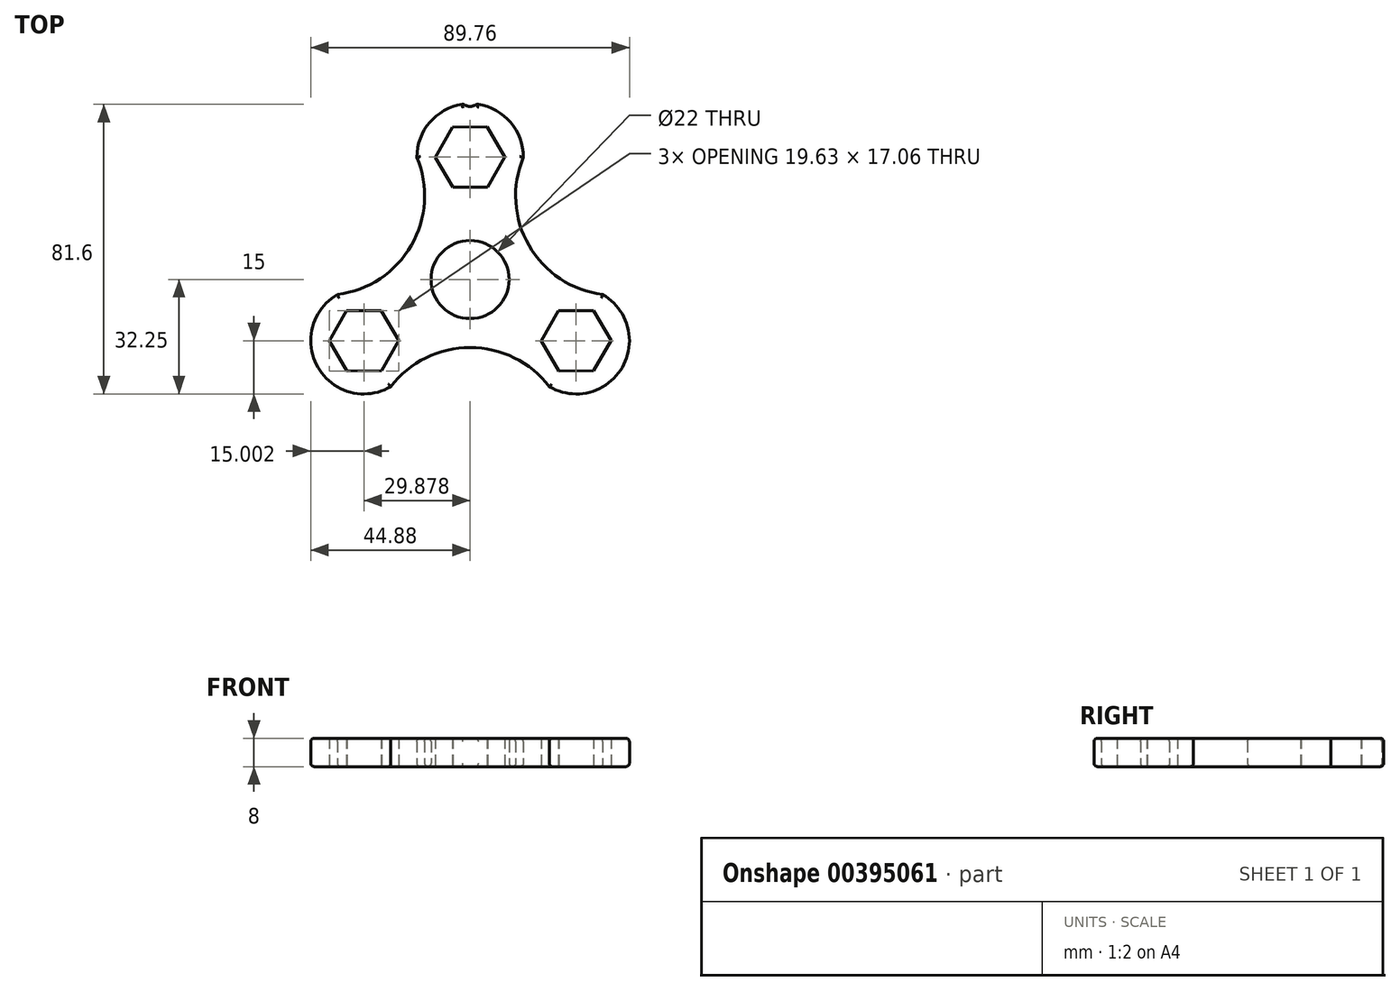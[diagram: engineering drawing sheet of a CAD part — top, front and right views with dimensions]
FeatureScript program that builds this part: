
annotation { "Feature Type Name" : "Feature", "Feature Type Description" : "" }
export const myFeature = defineFeature(function(context is Context, id is Id, definition is map)
    precondition{}
    {
        {
            var Q0;
            Q0=qCreatedBy(makeId("Top.planeOp"),FACE);
            var sketch = newSketch(context, id + "F0", { "sketchPlane" : qUnion([Q0])});
            skCircle(sketch, "E0", {"center": v(0, 0) * mm, "radius": 11 * mm});
            skCircle(sketch, "E1.cCircle", {"center": v(0, 34.5) * mm, "radius": 8.5 * mm, "construction": true});
            skLineSegment(sketch, "E1.0", {"start": v(9.81, 34.56) * mm, "end": v(4.96, 26.03) * mm});
            skLineSegment(sketch, "E1.1", {"start": v(4.96, 26.03) * mm, "end": v(-4.86, 25.97) * mm});
            skLineSegment(sketch, "E1.2", {"start": v(-4.86, 25.97) * mm, "end": v(-9.81, 34.44) * mm});
            skLineSegment(sketch, "E1.3", {"start": v(-9.81, 34.44) * mm, "end": v(-4.96, 42.97) * mm});
            skLineSegment(sketch, "E1.4", {"start": v(-4.96, 42.97) * mm, "end": v(4.86, 43.03) * mm});
            skLineSegment(sketch, "E1.5", {"start": v(4.86, 43.03) * mm, "end": v(9.81, 34.56) * mm});
            skPoint(sketch, "E1.0.midPoint", {"position": v(7.39, 30.3) * mm});
            skArc(sketch, "E2", {"start": v(15, 34.44) * mm, "mid": v(0, 49.5) * mm, "end": v(-15, 34.44) * mm});
            skArc(sketch, "E3.1.0", {"start": v(-37.33, -4.23) * mm, "mid": v(-42.87, -24.75) * mm, "end": v(-22.33, -30.21) * mm});
            skLineSegment(sketch, "E3.1.3", {"start": v(-34.84, -8.78) * mm, "end": v(-25.02, -8.72) * mm});
            skLineSegment(sketch, "E3.1.4", {"start": v(-39.7, -17.31) * mm, "end": v(-34.84, -8.78) * mm});
            skLineSegment(sketch, "E3.1.5", {"start": v(-34.73, -25.78) * mm, "end": v(-39.7, -17.31) * mm});
            skLineSegment(sketch, "E3.1.6", {"start": v(-24.92, -25.72) * mm, "end": v(-34.73, -25.78) * mm});
            skLineSegment(sketch, "E3.1.7", {"start": v(-20.06, -17.19) * mm, "end": v(-24.92, -25.72) * mm});
            skLineSegment(sketch, "E3.1.8", {"start": v(-25.02, -8.72) * mm, "end": v(-20.06, -17.19) * mm});
            skArc(sketch, "E3.2.0", {"start": v(22.33, -30.21) * mm, "mid": v(42.87, -24.75) * mm, "end": v(37.33, -4.23) * mm});
            skLineSegment(sketch, "E3.2.3", {"start": v(25.02, -25.78) * mm, "end": v(20.06, -17.31) * mm});
            skLineSegment(sketch, "E3.2.4", {"start": v(34.84, -25.72) * mm, "end": v(25.02, -25.78) * mm});
            skLineSegment(sketch, "E3.2.5", {"start": v(39.7, -17.19) * mm, "end": v(34.84, -25.72) * mm});
            skLineSegment(sketch, "E3.2.6", {"start": v(34.73, -8.72) * mm, "end": v(39.7, -17.19) * mm});
            skLineSegment(sketch, "E3.2.7", {"start": v(24.92, -8.78) * mm, "end": v(34.73, -8.72) * mm});
            skLineSegment(sketch, "E3.2.8", {"start": v(20.06, -17.31) * mm, "end": v(24.92, -8.78) * mm});
            skPoint(sketch, "E4.MirrorCS.start.orphan", {"position": v(13.42, 9.6) * mm});
            skPoint(sketch, "E5.start.orphan", {"position": v(-13.42, 9.6) * mm});
            skArc(sketch, "E6", {"start": v(15, 34.44) * mm, "mid": v(16.59, 9.58) * mm, "end": v(37.33, -4.23) * mm});
            skArc(sketch, "E7.1.0", {"start": v(-37.33, -4.23) * mm, "mid": v(-16.59, 9.58) * mm, "end": v(-15, 34.44) * mm});
            skArc(sketch, "E7.2.0", {"start": v(22.33, -30.21) * mm, "mid": v(0, -19.15) * mm, "end": v(-22.33, -30.21) * mm});
            skSolve(sketch);
        }
        {
            var Q0;
            Q0=makeQuery(id+"F0.imprint","IMPRINT",FACE,{"disambiguationData":[TD([[makeQuery(id+"F0.imprint","IMPRINT",EDGE,{"derivedFrom":sQuery(id+"F0.wireOp",EDGE,"E3.1.0")}),1.0]])]});
            var Q1;
            Q1=makeQuery(id+"F0.imprint","IMPRINT",FACE,{"disambiguationData":[TD([[makeQuery(id+"F0.imprint","IMPRINT",EDGE,{"derivedFrom":sQuery(id+"F0.wireOp",EDGE,"E3.2.0")}),1.0]])]});
            var Q2;
            Q2=makeQuery(id+"F0.imprint","IMPRINT",FACE,{"disambiguationData":[TD([[makeQuery(id+"F0.imprint","IMPRINT",EDGE,{"derivedFrom":sQuery(id+"F0.wireOp",EDGE,"E0")}),-1.0]])]});
            var Q3;
            Q3=makeQuery(id+"F0.imprint","IMPRINT",FACE,{"disambiguationData":[TD([[makeQuery(id+"F0.imprint","IMPRINT",EDGE,{"derivedFrom":sQuery(id+"F0.wireOp",EDGE,"E1.0")}),1.0]])]});
            extrude(context, id + "F1", {"entities" : qUnion([Q0, Q1, Q2, Q3]), "depth" : 8 * mm});
        }
        {
            var Q0;
            Q0=makeQuery(id+"F1.opExtrude","CAP_EDGE",EDGE,{"disambiguationData":[OSD([sQuery(id+"F0.wireOp",EDGE,"E0")])],"isStart":false});
            var Q1;
            {var subQ0=sQuery(id+"F0.wireOp",EDGE,"kYvrFP9H-Q7yO-7neS-k9Bp-IsUak0FltTsv");Q1=makeQuery(id+"F1.opExtrude","CAP_EDGE",EDGE,{"disambiguationData":[OSD([subQ0]),TDD([makeQuery(id+"F0.imprint","IMPRINT",EDGE,{"disambiguationData":[TD([[makeQuery(id+"F0.imprint","INTERSECT",VERTEX,{"derivedFrom":[subQ0,sQuery(id+"F0.wireOp",EDGE,"E5")]}),-1.0]])],"derivedFrom":subQ0})])],"isStart":false});}
            var Q2;
            Q2=makeQuery(id+"F1.opExtrude","CAP_EDGE",EDGE,{"disambiguationData":[OSD([sQuery(id+"F0.wireOp",EDGE,"E5")])],"isStart":false});
            var Q3;
            Q3=makeQuery(id+"F1.opExtrude","CAP_EDGE",EDGE,{"disambiguationData":[OSD([sQuery(id+"F0.wireOp",EDGE,"E3.1.2")])],"isStart":false});
            var Q4;
            Q4=makeQuery(id+"F1.opExtrude","CAP_EDGE",EDGE,{"disambiguationData":[OSD([sQuery(id+"F0.wireOp",EDGE,"E2")])],"isStart":false});
            var Q5;
            Q5=makeQuery(id+"F1.opExtrude","CAP_EDGE",EDGE,{"disambiguationData":[OSD([sQuery(id+"F0.wireOp",EDGE,"E4.MirrorCS")])],"isStart":false});
            var Q6;
            {var subQ0=sQuery(id+"F0.wireOp",EDGE,"kYvrFP9H-Q7yO-7neS-k9Bp-IsUak0FltTsv");Q6=makeQuery(id+"F1.opExtrude","CAP_EDGE",EDGE,{"disambiguationData":[OSD([subQ0]),TDD([makeQuery(id+"F0.imprint","IMPRINT",EDGE,{"disambiguationData":[TD([[makeQuery(id+"F0.imprint","INTERSECT",VERTEX,{"derivedFrom":[subQ0,sQuery(id+"F0.wireOp",EDGE,"E4.MirrorCS")]}),1.0]])],"derivedFrom":subQ0})])],"isStart":false});}
            var Q7;
            Q7=makeQuery(id+"F1.opExtrude","CAP_EDGE",EDGE,{"disambiguationData":[OSD([sQuery(id+"F0.wireOp",EDGE,"E3.2.1")])],"isStart":false});
            var Q8;
            Q8=makeQuery(id+"F1.opExtrude","CAP_EDGE",EDGE,{"disambiguationData":[OSD([sQuery(id+"F0.wireOp",EDGE,"E3.2.0")])],"isStart":false});
            var Q9;
            Q9=makeQuery(id+"F1.opExtrude","CAP_EDGE",EDGE,{"disambiguationData":[OSD([sQuery(id+"F0.wireOp",EDGE,"E3.2.2")])],"isStart":false});
            var Q10;
            {var subQ0=sQuery(id+"F0.wireOp",EDGE,"kYvrFP9H-Q7yO-7neS-k9Bp-IsUak0FltTsv");Q10=makeQuery(id+"F1.opExtrude","CAP_EDGE",EDGE,{"disambiguationData":[OSD([subQ0]),TDD([makeQuery(id+"F0.imprint","IMPRINT",EDGE,{"disambiguationData":[TD([[makeQuery(id+"F0.imprint","INTERSECT",VERTEX,{"derivedFrom":[subQ0,sQuery(id+"F0.wireOp",EDGE,"E3.1.1")]}),-1.0]])],"derivedFrom":subQ0})])],"isStart":false});}
            var Q11;
            Q11=makeQuery(id+"F1.opExtrude","CAP_EDGE",EDGE,{"disambiguationData":[OSD([sQuery(id+"F0.wireOp",EDGE,"E3.1.1")])],"isStart":false});
            var Q12;
            Q12=makeQuery(id+"F1.opExtrude","CAP_EDGE",EDGE,{"disambiguationData":[OSD([sQuery(id+"F0.wireOp",EDGE,"E3.1.0")])],"isStart":false});
            var Q13;
            Q13=makeQuery(id+"F1.opExtrude","CAP_EDGE",EDGE,{"disambiguationData":[OSD([sQuery(id+"F0.wireOp",EDGE,"E3.2.2")])],"isStart":true});
            var Q14;
            {var subQ0=sQuery(id+"F0.wireOp",EDGE,"kYvrFP9H-Q7yO-7neS-k9Bp-IsUak0FltTsv");Q14=makeQuery(id+"F1.opExtrude","CAP_EDGE",EDGE,{"disambiguationData":[OSD([subQ0]),TDD([makeQuery(id+"F0.imprint","IMPRINT",EDGE,{"disambiguationData":[TD([[makeQuery(id+"F0.imprint","INTERSECT",VERTEX,{"derivedFrom":[subQ0,sQuery(id+"F0.wireOp",EDGE,"E3.1.1")]}),-1.0]])],"derivedFrom":subQ0})])],"isStart":true});}
            var Q15;
            Q15=makeQuery(id+"F1.opExtrude","CAP_EDGE",EDGE,{"disambiguationData":[OSD([sQuery(id+"F0.wireOp",EDGE,"E3.1.1")])],"isStart":true});
            var Q16;
            Q16=makeQuery(id+"F1.opExtrude","CAP_EDGE",EDGE,{"disambiguationData":[OSD([sQuery(id+"F0.wireOp",EDGE,"E3.1.0")])],"isStart":true});
            var Q17;
            Q17=makeQuery(id+"F1.opExtrude","CAP_EDGE",EDGE,{"disambiguationData":[OSD([sQuery(id+"F0.wireOp",EDGE,"E3.1.2")])],"isStart":true});
            var Q18;
            {var subQ0=sQuery(id+"F0.wireOp",EDGE,"kYvrFP9H-Q7yO-7neS-k9Bp-IsUak0FltTsv");Q18=makeQuery(id+"F1.opExtrude","CAP_EDGE",EDGE,{"disambiguationData":[OSD([subQ0]),TDD([makeQuery(id+"F0.imprint","IMPRINT",EDGE,{"disambiguationData":[TD([[makeQuery(id+"F0.imprint","INTERSECT",VERTEX,{"derivedFrom":[subQ0,sQuery(id+"F0.wireOp",EDGE,"E5")]}),-1.0]])],"derivedFrom":subQ0})])],"isStart":true});}
            var Q19;
            Q19=makeQuery(id+"F1.opExtrude","CAP_EDGE",EDGE,{"disambiguationData":[OSD([sQuery(id+"F0.wireOp",EDGE,"E5")])],"isStart":true});
            var Q20;
            Q20=makeQuery(id+"F1.opExtrude","CAP_EDGE",EDGE,{"disambiguationData":[OSD([sQuery(id+"F0.wireOp",EDGE,"E2")])],"isStart":true});
            var Q21;
            Q21=makeQuery(id+"F1.opExtrude","CAP_EDGE",EDGE,{"disambiguationData":[OSD([sQuery(id+"F0.wireOp",EDGE,"E4.MirrorCS")])],"isStart":true});
            var Q22;
            {var subQ0=sQuery(id+"F0.wireOp",EDGE,"kYvrFP9H-Q7yO-7neS-k9Bp-IsUak0FltTsv");Q22=makeQuery(id+"F1.opExtrude","CAP_EDGE",EDGE,{"disambiguationData":[OSD([subQ0]),TDD([makeQuery(id+"F0.imprint","IMPRINT",EDGE,{"disambiguationData":[TD([[makeQuery(id+"F0.imprint","INTERSECT",VERTEX,{"derivedFrom":[subQ0,sQuery(id+"F0.wireOp",EDGE,"E4.MirrorCS")]}),1.0]])],"derivedFrom":subQ0})])],"isStart":true});}
            var Q23;
            Q23=makeQuery(id+"F1.opExtrude","CAP_EDGE",EDGE,{"disambiguationData":[OSD([sQuery(id+"F0.wireOp",EDGE,"E3.2.1")])],"isStart":true});
            var Q24;
            Q24=makeQuery(id+"F1.opExtrude","CAP_EDGE",EDGE,{"disambiguationData":[OSD([sQuery(id+"F0.wireOp",EDGE,"E0")])],"isStart":true});
            var Q25;
            Q25=makeQuery(id+"F1.opExtrude","CAP_EDGE",EDGE,{"disambiguationData":[OSD([sQuery(id+"F0.wireOp",EDGE,"E7.2.0")])],"isStart":false});
            var Q26;
            Q26=makeQuery(id+"F1.opExtrude","CAP_EDGE",EDGE,{"disambiguationData":[OSD([sQuery(id+"F0.wireOp",EDGE,"E6")])],"isStart":true});
            var Q27;
            Q27=makeQuery(id+"F1.opExtrude","CAP_EDGE",EDGE,{"disambiguationData":[OSD([sQuery(id+"F0.wireOp",EDGE,"E7.1.0")])],"isStart":true});
            var Q28;
            Q28=makeQuery(id+"F1.opExtrude","CAP_EDGE",EDGE,{"disambiguationData":[OSD([sQuery(id+"F0.wireOp",EDGE,"E7.1.0")])],"isStart":false});
            var Q29;
            Q29=makeQuery(id+"F1.opExtrude","CAP_EDGE",EDGE,{"disambiguationData":[OSD([sQuery(id+"F0.wireOp",EDGE,"E6")])],"isStart":false});
            var Q30;
            Q30=makeQuery(id+"F1.opExtrude","CAP_EDGE",EDGE,{"disambiguationData":[OSD([sQuery(id+"F0.wireOp",EDGE,"E7.2.0")])],"isStart":true});
            var Q31;
            Q31=makeQuery(id+"F1.opExtrude","CAP_EDGE",EDGE,{"disambiguationData":[OSD([sQuery(id+"F0.wireOp",EDGE,"E3.2.0")])],"isStart":true});
            fillet(context, id + "F2", {"entities" : qUnion([Q0, Q1, Q2, Q3, Q4, Q5, Q6, Q7, Q8, Q9, Q10, Q11, Q12, Q13, Q14, Q15, Q16, Q17, Q18, Q19, Q20, Q21, Q22, Q23, Q24, Q25, Q26, Q27, Q28, Q29, Q30, Q31]), "radius" : 1 * mm, "tangentPropagation" : true, "allowEdgeOverflow" : false});
        }
        {
            var Q0;
            Q0=qCreatedBy(makeId("Top.planeOp"),FACE);
            var sketch = newSketch(context, id + "F3", { "sketchPlane" : qUnion([Q0])});
            skCircle(sketch, "E8", {"center": v(0, 51.82) * mm, "radius": 3.04 * mm});
            skSolve(sketch);
        }
        {
            var Q0;
            Q0=makeQuery(id+"F3.imprint","IMPRINT",FACE,{"disambiguationData":[TD([[makeQuery(id+"F3.imprint","IMPRINT",EDGE,{"derivedFrom":sQuery(id+"F3.wireOp",EDGE,"E8")}),1.0]])]});
            extrude(context, id + "F4", {"entities" : qUnion([Q0]), "operationType" : NewBodyOperationType.REMOVE, "depth" : 19 * mm});
        }
        {
            var Q0;
            Q0=makeQuery(id+"F4.boolean.opBoolean","INTERSECT",EDGE,{"disambiguationData":[OD(1.0)],"derivedFrom":[makeQuery(id+"F1.opExtrude","SWEPT_FACE",FACE,{"disambiguationData":[OSD([sQuery(id+"F0.wireOp",EDGE,"E2")])]}),makeQuery(id+"F4.opExtrude","SWEPT_FACE",FACE,{"disambiguationData":[OSD([sQuery(id+"F3.wireOp",EDGE,"E8")])]})]});
            var Q1;
            Q1=makeQuery(id+"F4.boolean.opBoolean","INTERSECT",EDGE,{"disambiguationData":[OD(0.0)],"derivedFrom":[makeQuery(id+"F1.opExtrude","SWEPT_FACE",FACE,{"disambiguationData":[OSD([sQuery(id+"F0.wireOp",EDGE,"E2")])]}),makeQuery(id+"F4.opExtrude","SWEPT_FACE",FACE,{"disambiguationData":[OSD([sQuery(id+"F3.wireOp",EDGE,"E8")])]})]});
            var Q2;
            {var subQ0=sQuery(id+"F0.wireOp",EDGE,"E2");Q2=makeQuery(id+"F4.boolean.opBoolean","INTERSECT",EDGE,{"derivedFrom":[makeQuery(id+"F2.opFillet","BLEND_FACE",FACE,{"disambiguationData":[OSD([subQ0]),TDD([makeQuery(id+"F1.opExtrude","CAP_EDGE",EDGE,{"disambiguationData":[OSD([subQ0])],"isStart":false})])]}),makeQuery(id+"F4.opExtrude","SWEPT_FACE",FACE,{"disambiguationData":[OSD([sQuery(id+"F3.wireOp",EDGE,"E8")])]})]});}
            var Q3;
            {var subQ0=sQuery(id+"F0.wireOp",EDGE,"E2");Q3=makeQuery(id+"F4.boolean.opBoolean","INTERSECT",EDGE,{"derivedFrom":[makeQuery(id+"F2.opFillet","BLEND_FACE",FACE,{"disambiguationData":[OSD([subQ0]),TDD([makeQuery(id+"F1.opExtrude","CAP_EDGE",EDGE,{"disambiguationData":[OSD([subQ0])],"isStart":true})])]}),makeQuery(id+"F4.opExtrude","SWEPT_FACE",FACE,{"disambiguationData":[OSD([sQuery(id+"F3.wireOp",EDGE,"E8")])]})]});}
            fillet(context, id + "F5", {"entities" : qUnion([Q0, Q1, Q2, Q3]), "radius" : 1 * mm, "tangentPropagation" : true, "allowEdgeOverflow" : false});
        }
    });
